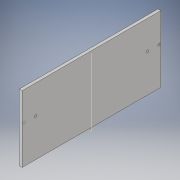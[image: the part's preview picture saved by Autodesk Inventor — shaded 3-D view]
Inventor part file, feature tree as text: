
AUTODESK INVENTOR PART (.ipt)
format: ipt  version: 2017 (Build 210142000, 142)  size: 105,984 bytes
history: native  units: in
note: dims shown in document units (in); Inventor stores cm internally (conversion verified against a paired STEP export)
features: sketch x2, extrude x1, hole x1, plane x1, projected_geometry x1
ambient origin geometry x8: Origin, YZ Plane, XZ Plane, XY Plane, X Axis, Y Axis, Z Axis, Center Point
bodies: Solid1 (feature_tree)
feature tree (6):
  extrude  "Extrusion1"  Depth=9.125in
  hole  "Hole1"  [1 undecoded]
  plane  "Work Plane1"
  sketch  "Sketch1"  dims[d0=4.375in d1=9.125in]
  sketch  "Sketch2"  dims[d2=0.1875in d3=0.0in d4=2.5in d5=2.5in d6=2.5in d7=2.5in d8=0.125in d9=0.75in d10=0.75in d11=0.125in d12=0.145in d13=0.75in d14=0.75in d15=0.188in d16=0.5635in d17=1.0in d18=0.8108in]
  projected_geometry  "Projected Loop1"
note: 1 required parameter value undecoded (feature->parameter linkage not recoverable at this tier; creation-order binding heuristic only, values carry confidence <= 0.55)
